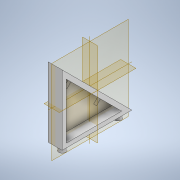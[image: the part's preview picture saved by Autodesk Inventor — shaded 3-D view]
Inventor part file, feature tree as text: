
AUTODESK INVENTOR PART (.ipt)
format: ipt  version: 2022.4 (Build 264492010, 492A)  size: 146,944 bytes
history: native  units: mm
features: extrude x4, sketch x4, mirror x1
ambient origin geometry x8: Origin, YZ Plane, XZ Plane, XY Plane, X Axis, Y Axis, Z Axis, Center Point
bodies: Solid1 (feature_tree)
feature tree (9):
  extrude  "Extrusion1"  Depth=50.0mm
  extrude  "Extrusion2"  Depth=3.0mm
  extrude  "Extrusion3"  Depth=5.0mm
  extrude  "Extrusion4"  Depth=10.0mm
  mirror  "Mirror1"
  sketch  "Sketch2"  dims[d0=50.0mm d1=50.0mm]
  sketch  "Sketch4"  dims[d2=10.0mm d3=0.0mm d8=3.0mm]
  sketch  "Sketch5"  dims[d9=7.0mm d10=0.0mm d11=5.0mm]
  sketch  "Sketch8"  dims[d12=5.0mm d13=20.0mm d15=40.0mm d16=10.0mm d18=10.0mm d20=5.0mm d21=0.0mm d31=70.710678mm d32=5.0mm d34=15.0mm d35=7.0mm d36=0.0mm]
